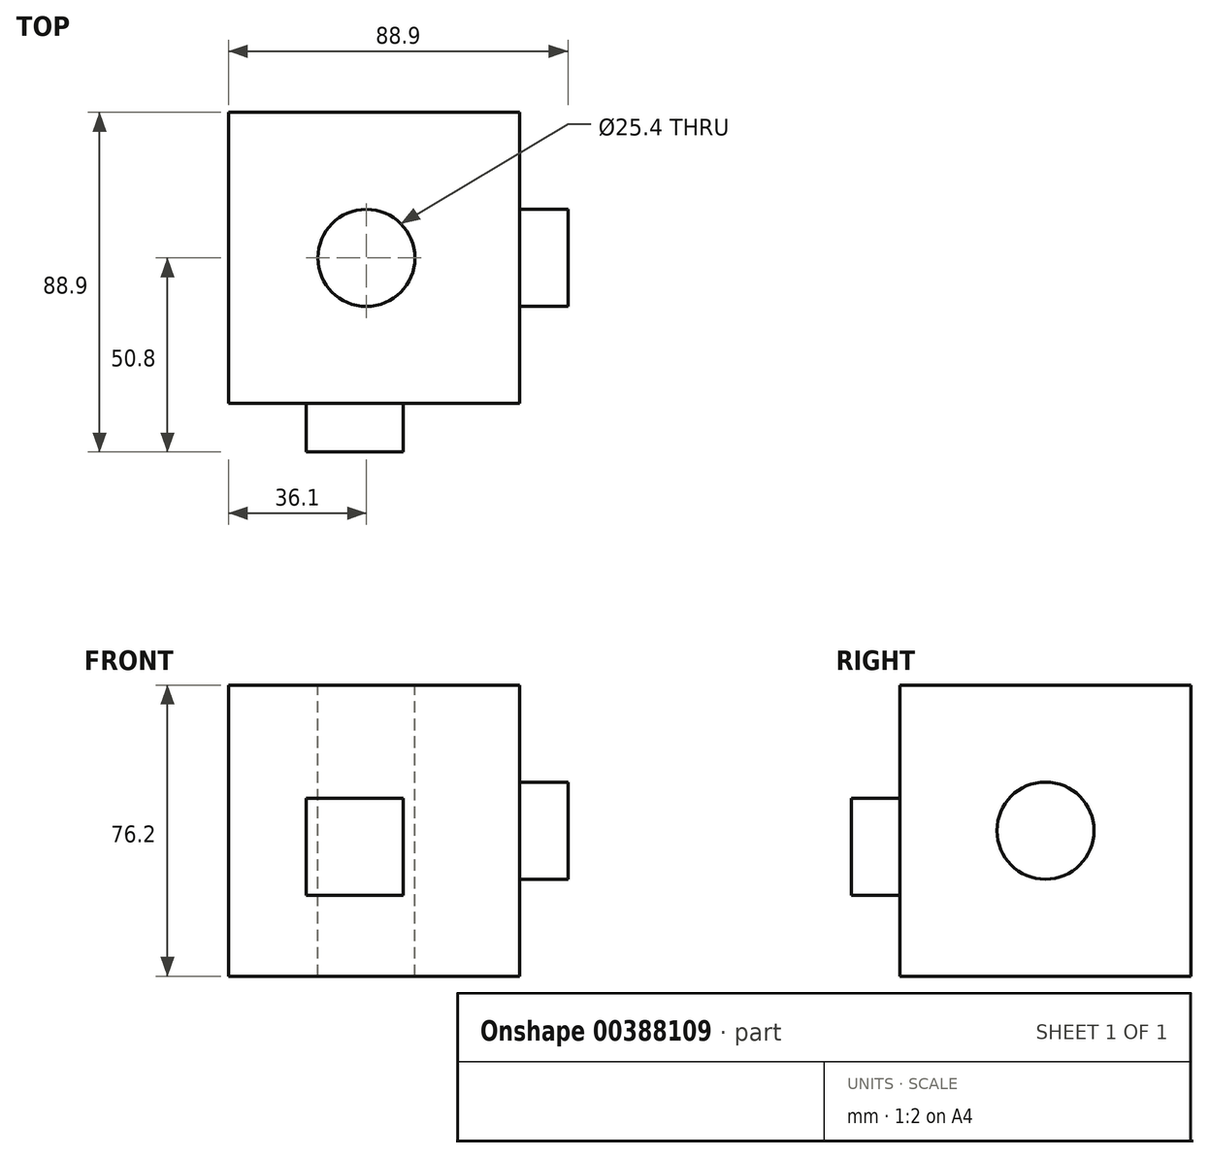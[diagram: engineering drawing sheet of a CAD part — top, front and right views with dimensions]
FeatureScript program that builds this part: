
annotation { "Feature Type Name" : "Feature", "Feature Type Description" : "" }
export const myFeature = defineFeature(function(context is Context, id is Id, definition is map)
    precondition{}
    {
        {
            var Q0;
            Q0=qCreatedBy(makeId("Front.planeOp"),FACE);
            var sketch = newSketch(context, id + "F0", { "sketchPlane" : qUnion([Q0])});
            skLineSegment(sketch, "E0.bottom", {"start": v(-36.1, 49.93) * mm, "end": v(40.1, 49.93) * mm});
            skLineSegment(sketch, "E0.top", {"start": v(-36.1, -26.27) * mm, "end": v(40.1, -26.27) * mm});
            skLineSegment(sketch, "E0.left", {"start": v(-36.1, 49.93) * mm, "end": v(-36.1, -26.27) * mm});
            skLineSegment(sketch, "E0.right", {"start": v(40.1, 49.93) * mm, "end": v(40.1, -26.27) * mm});
            skSolve(sketch);
        }
        {
            var Q0;
            Q0=makeQuery(id+"F0.imprint","IMPRINT",FACE,{"disambiguationData":[TD([[makeQuery(id+"F0.imprint","IMPRINT",EDGE,{"derivedFrom":sQuery(id+"F0.wireOp",EDGE,"E0.bottom")}),-1.0]])]});
            extrude(context, id + "F1", {"entities" : qUnion([Q0]), "depth" : 76.2 * mm});
        }
        {
            var Q0;
            Q0=makeQuery(id+"F1.opExtrude","SWEPT_FACE",FACE,{"disambiguationData":[OSD([sQuery(id+"F0.wireOp",EDGE,"E0.bottom")])]});
            var sketch = newSketch(context, id + "F2", { "sketchPlane" : qUnion([Q0])});
            skPoint(sketch, "E1", {"position": v(0, -38.1) * mm});
            skSolve(sketch);
        }
        {
            var Q0;
            Q0=sQuery(id+"F2.wireOp",VERTEX,"E1");
            var Q1;
            Q1=makeQuery(id+"F1.opExtrude","SWEPT_BODY",BODY,{"disambiguationData":[OSD([sQuery(id+"F0.wireOp",EDGE,"E0.bottom"),sQuery(id+"F0.wireOp",EDGE,"E0.top"),sQuery(id+"F0.wireOp",EDGE,"E0.left"),sQuery(id+"F0.wireOp",EDGE,"E0.right")])]});
            hole(context, id + "F3", {"style" : HoleStyle.SIMPLE, "endStyle" : HoleEndStyle.THROUGH, "holeDiameter" : 25.4 * mm, "isTappedThrough" : true, "tappedDepth" : 12.7 * mm, "tapClearance" : 3, "locations" : qUnion([Q0]), "scope" : qUnion([Q1])});
        }
        {
            var Q0;
            Q0=makeQuery(id+"F1.opExtrude","CAP_FACE",FACE,{"disambiguationData":[OSD([sQuery(id+"F0.wireOp",EDGE,"E0.bottom"),sQuery(id+"F0.wireOp",EDGE,"E0.top"),sQuery(id+"F0.wireOp",EDGE,"E0.left"),sQuery(id+"F0.wireOp",EDGE,"E0.right")])],"isStart":false});
            var sketch = newSketch(context, id + "F4", { "sketchPlane" : qUnion([Q0])});
            skLineSegment(sketch, "E2.bottom", {"start": v(-15.8, 20.3) * mm, "end": v(9.6, 20.3) * mm});
            skLineSegment(sketch, "E2.top", {"start": v(-15.8, -5.1) * mm, "end": v(9.6, -5.1) * mm});
            skLineSegment(sketch, "E2.left", {"start": v(-15.8, 20.3) * mm, "end": v(-15.8, -5.1) * mm});
            skLineSegment(sketch, "E2.right", {"start": v(9.6, 20.3) * mm, "end": v(9.6, -5.1) * mm});
            skSolve(sketch);
        }
        {
            var Q0;
            Q0=makeQuery(id+"F4.imprint","IMPRINT",FACE,{"disambiguationData":[TD([[makeQuery(id+"F4.imprint","IMPRINT",EDGE,{"derivedFrom":sQuery(id+"F4.wireOp",EDGE,"E2.bottom")}),-1.0]])]});
            extrude(context, id + "F5", {"entities" : qUnion([Q0]), "operationType" : NewBodyOperationType.ADD, "depth" : 12.7 * mm});
        }
        {
            var Q0;
            Q0=makeQuery(id+"F1.opExtrude","SWEPT_FACE",FACE,{"disambiguationData":[OSD([sQuery(id+"F0.wireOp",EDGE,"E0.right")])]});
            var sketch = newSketch(context, id + "F6", { "sketchPlane" : qUnion([Q0])});
            skCircle(sketch, "E3", {"center": v(-38.1, 11.83) * mm, "radius": 12.7 * mm});
            skSolve(sketch);
        }
        {
            var Q0;
            Q0 = qSketchRegion(id + "F6", true);
            extrude(context, id + "F7", {"entities" : qUnion([Q0]), "operationType" : NewBodyOperationType.ADD, "depth" : 12.7 * mm});
        }
    });
